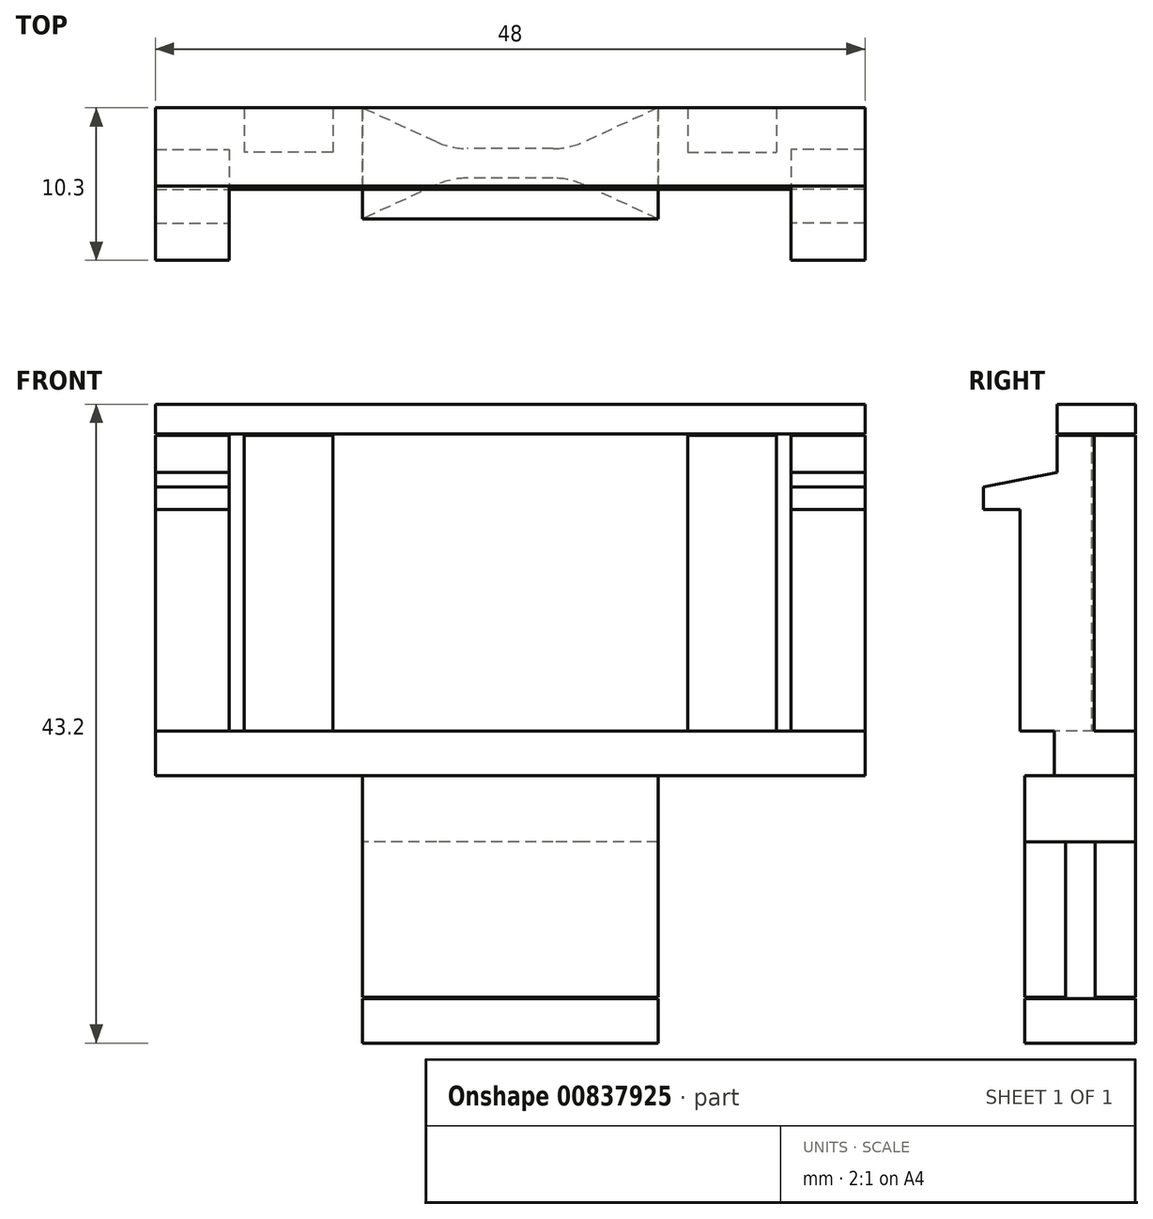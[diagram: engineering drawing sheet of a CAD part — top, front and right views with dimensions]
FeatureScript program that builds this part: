
annotation { "Feature Type Name" : "Feature", "Feature Type Description" : "" }
export const myFeature = defineFeature(function(context is Context, id is Id, definition is map)
    precondition{}
    {
        {
            var Q0;
            Q0=qCreatedBy(makeId("Top.planeOp"),FACE);
            var sketch = newSketch(context, id + "F0", { "sketchPlane" : qUnion([Q0])});
            skLineSegment(sketch, "E0.left", {"start": v(24, -2.75) * mm, "end": v(24, 2.75) * mm});
            skPoint(sketch, "E0.middle", {"position": v(0, 0) * mm});
            skLineSegment(sketch, "E1.bottom", {"start": v(-10, -4.75) * mm, "end": v(10, -4.75) * mm});
            skLineSegment(sketch, "E1.top", {"start": v(-10, 2.75) * mm, "end": v(10, 2.75) * mm});
            skLineSegment(sketch, "E1.left", {"start": v(-10, -4.75) * mm, "end": v(-10, 2.75) * mm});
            skLineSegment(sketch, "E1.right", {"start": v(10, -4.75) * mm, "end": v(10, 2.75) * mm});
            skLineSegment(sketch, "E2", {"start": v(0, -4.75) * mm, "end": v(0, 0) * mm});
            skLineSegment(sketch, "E3", {"start": v(24, 2.75) * mm, "end": v(10, 2.75) * mm});
            skLineSegment(sketch, "E4", {"start": v(24, -2.75) * mm, "end": v(10, -2.75) * mm});
            skLineSegment(sketch, "E5", {"start": v(10, -2.75) * mm, "end": v(-10, -2.75) * mm});
            skSolve(sketch);
        }
        {
            var Q0;
            Q0=makeQuery(id+"F0.imprint","IMPRINT",FACE,{"disambiguationData":[TD([[makeQuery(id+"F0.imprint","IMPRINT",EDGE,{"derivedFrom":sQuery(id+"F0.wireOp",EDGE,"E0.bottom")}),-1.0]])]});
            var Q1;
            {var subQ0=sQuery(id+"F0.wireOp",EDGE,"E0.right");Q1=makeQuery(id+"F0.imprint","IMPRINT",FACE,{"disambiguationData":[TD([[makeQuery(id+"F0.imprint","IMPRINT",EDGE,{"derivedFrom":subQ0}),-1.0]])]});}
            var Q2;
            {var subQ0=sQuery(id+"F0.wireOp",EDGE,"E0.left");Q2=makeQuery(id+"F0.imprint","IMPRINT",FACE,{"disambiguationData":[TD([[makeQuery(id+"F0.imprint","IMPRINT",EDGE,{"derivedFrom":subQ0}),1.0]])]});}
            var Q3;
            {var subQ1=sQuery(id+"F0.wireOp",EDGE,"E1.top");Q3=makeQuery(id+"F0.imprint","IMPRINT",FACE,{"disambiguationData":[TD([[makeQuery(id+"F0.imprint","IMPRINT",EDGE,{"derivedFrom":subQ1}),-1.0]])]});}
            extrude(context, id + "F1", {"entities" : qUnion([Q0, Q1, Q2, Q3]), "depth" : 3 * mm, "offsetDistance" : 25 * mm});
        }
        {
            var Q0;
            {var subQ0=sQuery(id+"F0.wireOp",EDGE,"E2");var subQ1=sQuery(id+"F0.wireOp",EDGE,"E0.bottom");var subQ2=makeQuery(id+"F0.imprint","INTERSECT",VERTEX,{"derivedFrom":[subQ1,subQ0]});Q0=makeQuery(id+"F0.imprint","IMPRINT",FACE,{"disambiguationData":[TD([[makeQuery(id+"F0.imprint","IMPRINT",EDGE,{"disambiguationData":[TD([[subQ2,-1.0]])],"derivedFrom":subQ1}),1.0]])]});}
            var Q1;
            {var subQ0=sQuery(id+"F0.wireOp",EDGE,"E1.right");var subQ1=sQuery(id+"F0.wireOp",EDGE,"E0.bottom");var subQ2=makeQuery(id+"F0.imprint","INTERSECT",VERTEX,{"derivedFrom":[subQ1,subQ0]});Q1=makeQuery(id+"F0.imprint","IMPRINT",FACE,{"disambiguationData":[TD([[makeQuery(id+"F0.imprint","IMPRINT",EDGE,{"disambiguationData":[TD([[subQ2,-1.0]])],"derivedFrom":subQ1}),1.0]])]});}
            var Q2;
            {var subQ0=sQuery(id+"F0.wireOp",EDGE,"E1.top");Q2=makeQuery(id+"F0.imprint","IMPRINT",FACE,{"disambiguationData":[TD([[makeQuery(id+"F0.imprint","IMPRINT",EDGE,{"derivedFrom":subQ0}),-1.0]])]});}
            var Q3;
            {var subQ0=sQuery(id+"F0.wireOp",EDGE,"E1.left");var subQ1=sQuery(id+"F0.wireOp",EDGE,"E1.bottom");var subQ2=makeQuery(id+"F0.imprint","INTERSECT",VERTEX,{"derivedFrom":[subQ1,subQ0]});Q3=makeQuery(id+"F0.imprint","IMPRINT",FACE,{"disambiguationData":[TD([[makeQuery(id+"F0.imprint","IMPRINT",EDGE,{"disambiguationData":[TD([[subQ2,-1.0]])],"derivedFrom":subQ1}),1.0]])]});}
            var Q4;
            {var subQ0=sQuery(id+"F0.wireOp",EDGE,"E1.right");var subQ1=sQuery(id+"F0.wireOp",EDGE,"E1.bottom");var subQ2=makeQuery(id+"F0.imprint","INTERSECT",VERTEX,{"derivedFrom":[subQ1,subQ0]});Q4=makeQuery(id+"F0.imprint","IMPRINT",FACE,{"disambiguationData":[TD([[makeQuery(id+"F0.imprint","IMPRINT",EDGE,{"disambiguationData":[TD([[subQ2,1.0]])],"derivedFrom":subQ1}),1.0]])]});}
            var Q5;
            Q5=sQuery(id+"F0.wireOp",EDGE,"E1.bottom");
            extrude(context, id + "F2", {"entities" : qUnion([Q0, Q1, Q2, Q3, Q4]), "operationType" : NewBodyOperationType.ADD, "surfaceEntities" : qUnion([Q5]), "oppositeDirection" : true, "depth" : 4.5 * mm, "offsetDistance" : 25 * mm});
        }
        {
            var Q0;
            Q0=makeQuery(id+"F2.opExtrude","CAP_FACE",FACE,{"disambiguationData":[OSD([sQuery(id+"F0.wireOp",EDGE,"E1.bottom"),sQuery(id+"F0.wireOp",EDGE,"E1.top"),sQuery(id+"F0.wireOp",EDGE,"E1.left"),sQuery(id+"F0.wireOp",EDGE,"E1.right")])],"isStart":false});
            var sketch = newSketch(context, id + "F3", { "sketchPlane" : qUnion([Q0])});
            skLineSegment(sketch, "E6", {"start": v(10, -2.75) * mm, "end": v(4, 0) * mm});
            skLineSegment(sketch, "E7", {"start": v(4, 0) * mm, "end": v(-4, 0) * mm});
            skLineSegment(sketch, "E8", {"start": v(-4, 0) * mm, "end": v(-10, -2.75) * mm});
            skLineSegment(sketch, "E9", {"start": v(0, -2.75) * mm, "end": v(0, 4.75) * mm});
            skLineSegment(sketch, "E10", {"start": v(10, 1) * mm, "end": v(-10, 1) * mm});
            skLineSegment(sketch, "E11.MirrorCS", {"start": v(10, 4.75) * mm, "end": v(4, 2) * mm});
            skLineSegment(sketch, "E12.MirrorCS", {"start": v(4, 2) * mm, "end": v(-4, 2) * mm});
            skLineSegment(sketch, "E13.MirrorCS", {"start": v(-4, 2) * mm, "end": v(-10, 4.75) * mm});
            skSolve(sketch);
        }
        {
            var Q0;
            {var subQ0=sQuery(id+"F3.wireOp",EDGE,"E6");Q0=makeQuery(id+"F3.imprint","IMPRINT",FACE,{"disambiguationData":[TD([[makeQuery(id+"F3.imprint","IMPRINT",EDGE,{"derivedFrom":subQ0}),1.0]])]});}
            var Q1;
            {var subQ0=sQuery(id+"F3.wireOp",EDGE,"E8");Q1=makeQuery(id+"F3.imprint","IMPRINT",FACE,{"disambiguationData":[TD([[makeQuery(id+"F3.imprint","IMPRINT",EDGE,{"derivedFrom":subQ0}),1.0]])]});}
            var Q2;
            {var subQ5=sQuery(id+"F3.wireOp",EDGE,"E11.MirrorCS");Q2=makeQuery(id+"F3.imprint","IMPRINT",FACE,{"disambiguationData":[TD([[makeQuery(id+"F3.imprint","IMPRINT",EDGE,{"derivedFrom":subQ5}),-1.0]])]});}
            var Q3;
            {var subQ5=sQuery(id+"F3.wireOp",EDGE,"E13.MirrorCS");Q3=makeQuery(id+"F3.imprint","IMPRINT",FACE,{"disambiguationData":[TD([[makeQuery(id+"F3.imprint","IMPRINT",EDGE,{"derivedFrom":subQ5}),-1.0]])]});}
            extrude(context, id + "F4", {"entities" : qUnion([Q0, Q1, Q2, Q3]), "operationType" : NewBodyOperationType.ADD, "depth" : 10.5 * mm, "offsetDistance" : 25 * mm});
        }
        {
            var Q0;
            Q0=makeQuery(id+"F1.opExtrude","CAP_FACE",FACE,{"disambiguationData":[OSD([sQuery(id+"F0.wireOp",EDGE,"E0.bottom"),sQuery(id+"F0.wireOp",EDGE,"E0.top"),sQuery(id+"F0.wireOp",EDGE,"E0.left"),sQuery(id+"F0.wireOp",EDGE,"E0.right"),sQuery(id+"F0.wireOp",EDGE,"E1.top")])],"isStart":false});
            var sketch = newSketch(context, id + "F5", { "sketchPlane" : qUnion([Q0])});
            skLineSegment(sketch, "E14.bottom", {"start": v(12, 2.75) * mm, "end": v(18, 2.75) * mm});
            skLineSegment(sketch, "E14.top", {"start": v(12, -0.25) * mm, "end": v(18, -0.25) * mm});
            skLineSegment(sketch, "E14.left", {"start": v(12, 2.75) * mm, "end": v(12, -0.25) * mm});
            skLineSegment(sketch, "E14.right", {"start": v(18, 2.75) * mm, "end": v(18, -0.25) * mm});
            skLineSegment(sketch, "E15.bottom", {"start": v(24, -0.05) * mm, "end": v(19, -0.05) * mm});
            skLineSegment(sketch, "E15.top", {"start": v(24, -5.05) * mm, "end": v(19, -5.05) * mm});
            skLineSegment(sketch, "E15.left", {"start": v(24, -0.05) * mm, "end": v(24, -5.05) * mm});
            skLineSegment(sketch, "E15.right", {"start": v(19, -0.05) * mm, "end": v(19, -5.05) * mm});
            skSolve(sketch);
        }
        {
            var Q0;
            Q0=makeQuery(id+"F5.imprint","IMPRINT",FACE,{"disambiguationData":[TD([[makeQuery(id+"F5.imprint","IMPRINT",EDGE,{"derivedFrom":sQuery(id+"F5.wireOp",EDGE,"E14.bottom")}),-1.0]])]});
            var Q1;
            {var subQ0=sQuery(id+"F5.wireOp",EDGE,"E15.bottom");Q1=makeQuery(id+"F5.imprint","IMPRINT",FACE,{"disambiguationData":[TD([[makeQuery(id+"F5.imprint","IMPRINT",EDGE,{"derivedFrom":subQ0}),1.0]])]});}
            var Q2;
            {var subQ0=sQuery(id+"F5.wireOp",EDGE,"E15.top");Q2=makeQuery(id+"F5.imprint","IMPRINT",FACE,{"disambiguationData":[TD([[makeQuery(id+"F5.imprint","IMPRINT",EDGE,{"derivedFrom":subQ0}),-1.0]])]});}
            var Q3;
            Q3=makeQuery(id+"F5.imprint","IMPRINT",FACE,{"disambiguationData":[TD([[makeQuery(id+"F5.imprint","IMPRINT",EDGE,{"derivedFrom":sQuery(id+"F5.wireOp",EDGE,"5ea3a386-2e72-4d6f-82df-83e3c4ea288f0.MirrorCS")}),-1.0]])]});
            var Q4;
            {var subQ0=sQuery(id+"F5.wireOp",EDGE,"6e2690fa-45c8-4787-880a-55a10225b8a60.MirrorCS");Q4=makeQuery(id+"F5.imprint","IMPRINT",FACE,{"disambiguationData":[TD([[makeQuery(id+"F5.imprint","IMPRINT",EDGE,{"derivedFrom":subQ0}),-1.0]])]});}
            var Q5;
            {var subQ0=sQuery(id+"F5.wireOp",EDGE,"0a7195a1-aad8-4bab-bf7f-33c16b91a9020.MirrorCS");Q5=makeQuery(id+"F5.imprint","IMPRINT",FACE,{"disambiguationData":[TD([[makeQuery(id+"F5.imprint","IMPRINT",EDGE,{"derivedFrom":subQ0}),1.0]])]});}
            var Q6;
            Q6=makeQuery(id+"F5.imprint","IMPRINT",FACE,{"disambiguationData":[TD([[makeQuery(id+"F5.imprint","IMPRINT",EDGE,{"derivedFrom":sQuery(id+"F5.wireOp",EDGE,"E14.bottom")}),1.0]])]});
            extrude(context, id + "F6", {"entities" : qUnion([Q0, Q1, Q2, Q3, Q4, Q5, Q6]), "operationType" : NewBodyOperationType.ADD, "depth" : 15 * mm, "offsetDistance" : 25 * mm});
        }
        {
            var Q0;
            Q0=makeQuery(id+"F6.opExtrude","CAP_FACE",FACE,{"disambiguationData":[OSD([sQuery(id+"F5.wireOp",EDGE,"E15.bottom"),sQuery(id+"F5.wireOp",EDGE,"E15.top"),sQuery(id+"F5.wireOp",EDGE,"E15.left"),sQuery(id+"F5.wireOp",EDGE,"E15.right")])],"isStart":false});
            var sketch = newSketch(context, id + "F7", { "sketchPlane" : qUnion([Q0])});
            skLineSegment(sketch, "E16.bottom", {"start": v(19, -0.05) * mm, "end": v(24, -0.05) * mm});
            skLineSegment(sketch, "E16.top", {"start": v(19, -2.55) * mm, "end": v(24, -2.55) * mm});
            skLineSegment(sketch, "E16.left", {"start": v(19, -0.05) * mm, "end": v(19, -2.55) * mm});
            skLineSegment(sketch, "E16.right", {"start": v(24, -0.05) * mm, "end": v(24, -2.55) * mm});
            skSolve(sketch);
        }
        {
            var Q0;
            Q0=makeQuery(id+"F7.imprint","IMPRINT",FACE,{"disambiguationData":[TD([[makeQuery(id+"F7.imprint","IMPRINT",EDGE,{"derivedFrom":sQuery(id+"F7.wireOp",EDGE,"e6cad59b-8b4a-41b5-838e-72c1b71bfee10.MirrorCS")}),1.0]])]});
            var Q1;
            Q1=makeQuery(id+"F6.opExtrude","CAP_FACE",FACE,{"disambiguationData":[OSD([sQuery(id+"F5.wireOp",EDGE,"5ea3a386-2e72-4d6f-82df-83e3c4ea288f0.MirrorCS"),sQuery(id+"F5.wireOp",EDGE,"cba0519a-8970-4dc6-bb50-976fce54e4630.MirrorCS"),sQuery(id+"F5.wireOp",EDGE,"64ce6bfb-654b-4831-a077-69f9ca763c0d0.MirrorCS"),sQuery(id+"F5.wireOp",EDGE,"2814ab19-4fc1-4c3a-880c-0dd651a3744e0.MirrorCS")])],"isStart":false});
            var Q2;
            Q2=makeQuery(id+"F6.opExtrude","CAP_FACE",FACE,{"disambiguationData":[OSD([sQuery(id+"F5.wireOp",EDGE,"E14.bottom"),sQuery(id+"F5.wireOp",EDGE,"E14.top"),sQuery(id+"F5.wireOp",EDGE,"E14.left"),sQuery(id+"F5.wireOp",EDGE,"E14.right")])],"isStart":false});
            var Q3;
            Q3=makeQuery(id+"F7.imprint","IMPRINT",FACE,{"disambiguationData":[TD([[makeQuery(id+"F7.imprint","IMPRINT",EDGE,{"derivedFrom":sQuery(id+"F7.wireOp",EDGE,"E16.bottom")}),1.0]])]});
            extrude(context, id + "F8", {"entities" : qUnion([Q0, Q1, Q2, Q3]), "operationType" : NewBodyOperationType.ADD, "depth" : 5 * mm, "offsetDistance" : 25 * mm});
        }
        {
            var Q0;
            Q0=makeQuery(id+"F8.boolean.opBoolean","MERGE",FACE,{"derivedFrom":[makeQuery(id+"F6.boolean.opBoolean","MERGE",FACE,{"derivedFrom":[makeQuery(id+"F1.opExtrude","SWEPT_FACE",FACE,{"disambiguationData":[OSD([sQuery(id+"F0.wireOp",EDGE,"E0.left")])]}),makeQuery(id+"F6.opExtrude","SWEPT_FACE",FACE,{"disambiguationData":[OSD([sQuery(id+"F5.wireOp",EDGE,"E15.left")])]})]}),makeQuery(id+"F8.opExtrude","SWEPT_FACE",FACE,{"disambiguationData":[OSD([sQuery(id+"F7.wireOp",EDGE,"E16.right")])]})]});
            var sketch = newSketch(context, id + "F9", { "sketchPlane" : qUnion([Q0])});
            skLineSegment(sketch, "E17.bottom", {"start": v(-2.55, 18) * mm, "end": v(-7.55, 18) * mm});
            skLineSegment(sketch, "E17.top", {"start": v(-2.55, 19.5) * mm, "end": v(-7.55, 19.5) * mm});
            skLineSegment(sketch, "E17.left", {"start": v(-2.55, 18) * mm, "end": v(-2.55, 19.5) * mm});
            skLineSegment(sketch, "E17.right", {"start": v(-7.55, 18) * mm, "end": v(-7.55, 19.5) * mm});
            skLineSegment(sketch, "E18", {"start": v(-7.55, 19.5) * mm, "end": v(-2.55, 20.5) * mm});
            skSolve(sketch);
        }
        {
            var Q0;
            Q0=makeQuery(id+"F9.imprint","IMPRINT",FACE,{"disambiguationData":[TD([[makeQuery(id+"F9.imprint","IMPRINT",EDGE,{"derivedFrom":sQuery(id+"F9.wireOp",EDGE,"E17.top")}),1.0]])]});
            var Q1;
            {var subQ0=sQuery(id+"F9.wireOp",EDGE,"E17.top");Q1=makeQuery(id+"F9.imprint","IMPRINT",FACE,{"disambiguationData":[TD([[makeQuery(id+"F9.imprint","IMPRINT",EDGE,{"derivedFrom":subQ0}),-1.0]])]});}
            extrude(context, id + "F10", {"entities" : qUnion([Q0, Q1]), "operationType" : NewBodyOperationType.ADD, "oppositeDirection" : true, "depth" : 5 * mm, "offsetDistance" : 25 * mm});
        }
        {
            var Q0;
            Q0=makeQuery(id+"F1.opExtrude","SWEPT_BODY",BODY,{"disambiguationData":[OSD([sQuery(id+"F0.wireOp",EDGE,"E0.left"),sQuery(id+"F0.wireOp",EDGE,"E1.bottom"),sQuery(id+"F0.wireOp",EDGE,"E1.top"),sQuery(id+"F0.wireOp",EDGE,"E1.left"),sQuery(id+"F0.wireOp",EDGE,"E1.right"),sQuery(id+"F0.wireOp",EDGE,"E3"),sQuery(id+"F0.wireOp",EDGE,"E4")])]});
            var Q1;
            Q1=qCreatedBy(makeId("Right.planeOp"),FACE);
            mirror(context, id + "F11", {"operationType" : NewBodyOperationType.ADD, "entities" : qUnion([Q0]), "mirrorPlane" : qUnion([Q1])});
        }
        {
            var Q0;
            Q0=makeQuery(id+"F4.opExtrude","SWEPT_EDGE",EDGE,{"disambiguationData":[OSD([sQuery(id+"F3.wireOp",EDGE,"E12.MirrorCS"),sQuery(id+"F3.wireOp",EDGE,"E13.MirrorCS")])]});
            var Q1;
            Q1=makeQuery(id+"F4.opExtrude","SWEPT_EDGE",EDGE,{"disambiguationData":[OSD([sQuery(id+"F3.wireOp",EDGE,"E11.MirrorCS"),sQuery(id+"F3.wireOp",EDGE,"E12.MirrorCS")])]});
            var Q2;
            Q2=makeQuery(id+"F4.opExtrude","SWEPT_EDGE",EDGE,{"disambiguationData":[OSD([sQuery(id+"F3.wireOp",EDGE,"E6"),sQuery(id+"F3.wireOp",EDGE,"E7")])]});
            var Q3;
            Q3=makeQuery(id+"F4.opExtrude","SWEPT_EDGE",EDGE,{"disambiguationData":[OSD([sQuery(id+"F3.wireOp",EDGE,"E7"),sQuery(id+"F3.wireOp",EDGE,"E8")])]});
            fillet(context, id + "F12", {"entities" : qUnion([Q0, Q1, Q2, Q3]), "radius" : 5 * mm, "tangentPropagation" : true, "allowEdgeOverflow" : false});
        }
        {
            var Q0;
            {var subQ0=sQuery(id+"F0.wireOp",EDGE,"E1.bottom");Q0=makeQuery(id+"F4.boolean.opBoolean","MERGE",FACE,{"derivedFrom":[makeQuery(id+"F2.opExtrude","SWEPT_FACE",FACE,{"disambiguationData":[OSD([subQ0])]}),makeQuery(id+"F4.opExtrude","SWEPT_FACE",FACE,{"disambiguationData":[OSD([subQ0])]})]});}
            var sketch = newSketch(context, id + "F13", { "sketchPlane" : qUnion([Q0])});
            skLineSegment(sketch, "E19.bottom", {"start": v(-10, -15.1) * mm, "end": v(10, -15.1) * mm});
            skLineSegment(sketch, "E19.top", {"start": v(-10, -18.1) * mm, "end": v(10, -18.1) * mm});
            skLineSegment(sketch, "E19.left", {"start": v(-10, -15.1) * mm, "end": v(-10, -18.1) * mm});
            skLineSegment(sketch, "E19.right", {"start": v(10, -15.1) * mm, "end": v(10, -18.1) * mm});
            skSolve(sketch);
        }
        {
            var Q0;
            Q0=makeQuery(id+"F13.imprint","IMPRINT",FACE,{"disambiguationData":[TD([[makeQuery(id+"F13.imprint","IMPRINT",EDGE,{"derivedFrom":sQuery(id+"F13.wireOp",EDGE,"E19.bottom")}),-1.0]])]});
            extrude(context, id + "F14", {"entities" : qUnion([Q0]), "oppositeDirection" : true, "depth" : 7.5 * mm, "offsetDistance" : 25 * mm});
        }
        {
            var Q0;
            Q0=makeQuery(id+"F8.opExtrude","SWEPT_FACE",FACE,{"disambiguationData":[OSD([sQuery(id+"F7.wireOp",EDGE,"E16.top")])]});
            var sketch = newSketch(context, id + "F15", { "sketchPlane" : qUnion([Q0])});
            skLineSegment(sketch, "E20.bottom", {"start": v(24, 23.1) * mm, "end": v(-24, 23.1) * mm});
            skLineSegment(sketch, "E20.top", {"start": v(24, 25.1) * mm, "end": v(-24, 25.1) * mm});
            skLineSegment(sketch, "E20.left", {"start": v(24, 23.1) * mm, "end": v(24, 25.1) * mm});
            skLineSegment(sketch, "E20.right", {"start": v(-24, 23.1) * mm, "end": v(-24, 25.1) * mm});
            skSolve(sketch);
        }
        {
            var Q0;
            Q0=makeQuery(id+"F15.imprint","IMPRINT",FACE,{"disambiguationData":[TD([[makeQuery(id+"F15.imprint","IMPRINT",EDGE,{"derivedFrom":sQuery(id+"F15.wireOp",EDGE,"E20.bottom")}),-1.0]])]});
            var Q1;
            Q1=makeQuery(id+"F8.opExtrude","CAP_FACE",FACE,{"disambiguationData":[OSD([sQuery(id+"F5.wireOp",EDGE,"E14.bottom"),sQuery(id+"F5.wireOp",EDGE,"E14.top"),sQuery(id+"F5.wireOp",EDGE,"E14.left"),sQuery(id+"F5.wireOp",EDGE,"E14.right")])],"isStart":false});
            extrude(context, id + "F16", {"entities" : qUnion([Q0]), "oppositeDirection" : true, "depth" : 5.3 * mm, "endBoundEntityFace" : qUnion([Q1]), "offsetDistance" : 25 * mm});
        }
    });
